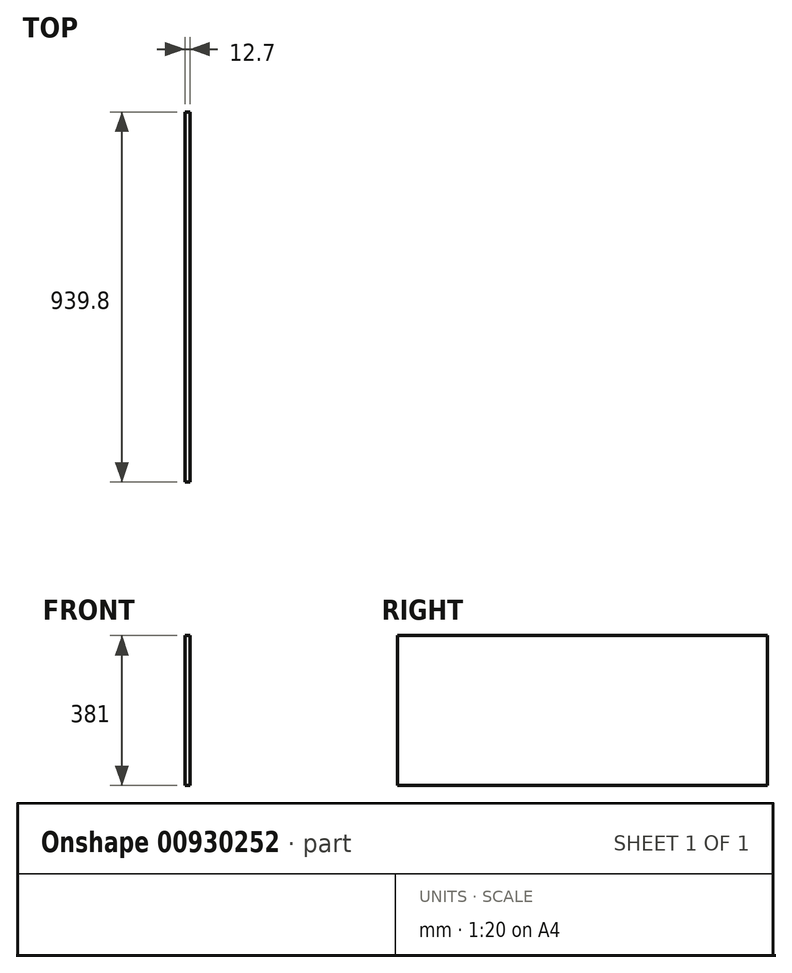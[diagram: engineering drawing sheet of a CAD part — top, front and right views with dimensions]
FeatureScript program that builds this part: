
annotation { "Feature Type Name" : "Feature", "Feature Type Description" : "" }
export const myFeature = defineFeature(function(context is Context, id is Id, definition is map)
    precondition{}
    {
        {
            var Q0;
            Q0=qCreatedBy(makeId("Right.planeOp"),FACE);
            var sketch = newSketch(context, id + "F0", { "sketchPlane" : qUnion([Q0])});
            skLineSegment(sketch, "E0.bottom", {"start": v(469.9, -190.5) * mm, "end": v(-469.9, -190.5) * mm});
            skLineSegment(sketch, "E0.top", {"start": v(469.9, 190.5) * mm, "end": v(-469.9, 190.5) * mm});
            skLineSegment(sketch, "E0.left", {"start": v(469.9, -190.5) * mm, "end": v(469.9, 190.5) * mm});
            skLineSegment(sketch, "E0.right", {"start": v(-469.9, -190.5) * mm, "end": v(-469.9, 190.5) * mm});
            skPoint(sketch, "E0.middle", {"position": v(0, 0) * mm});
            skSolve(sketch);
        }
        {
            var Q0;
            Q0=qSketchRegion(id+"F0",true);
            extrude(context, id + "F1", {"entities" : qUnion([Q0]), "endBound" : BoundingType.SYMMETRIC, "depth" : 12.7 * mm});
        }
    });
